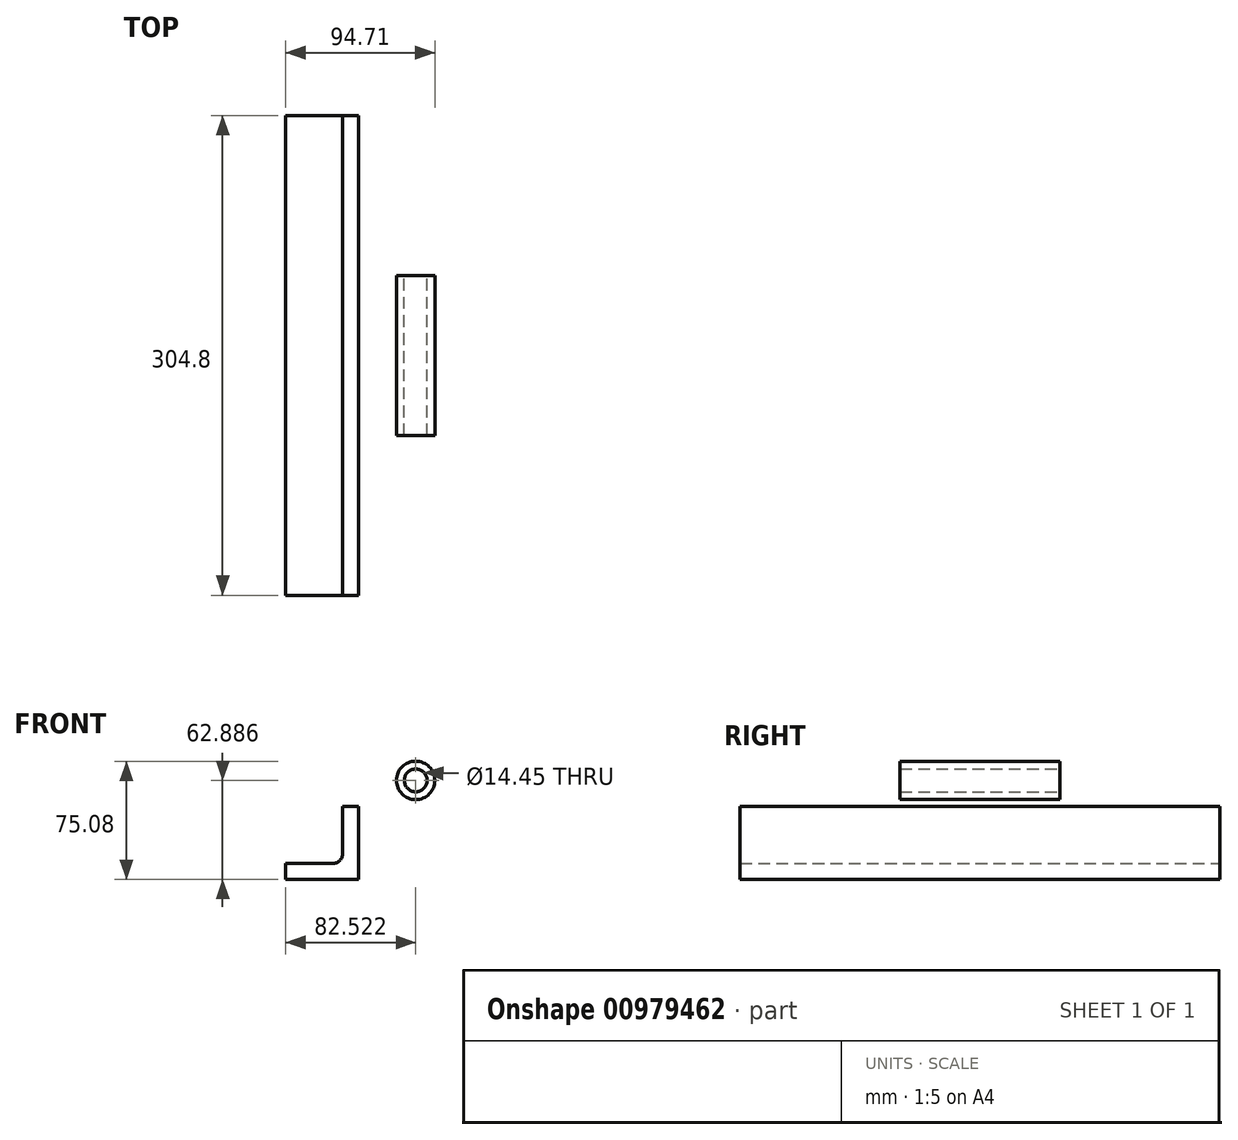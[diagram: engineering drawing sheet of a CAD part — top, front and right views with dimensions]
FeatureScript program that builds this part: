
annotation { "Feature Type Name" : "Feature", "Feature Type Description" : "" }
export const myFeature = defineFeature(function(context is Context, id is Id, definition is map)
    precondition{}
    {
        {
            var Q0;
            Q0=qCreatedBy(makeId("Front.planeOp"),FACE);
            var sketch = newSketch(context, id + "F0", { "sketchPlane" : qUnion([Q0])});
            skLineSegment(sketch, "E0.bottom", {"start": v(-46.24, 10.07) * mm, "end": v(-16.42, 10.07) * mm});
            skLineSegment(sketch, "E0.top", {"start": v(-46.24, 0) * mm, "end": v(0, 0) * mm});
            skLineSegment(sketch, "E0.left", {"start": v(-46.24, 10.07) * mm, "end": v(-46.24, 0) * mm});
            skLineSegment(sketch, "E0.right", {"start": v(0, 10.07) * mm, "end": v(0, 0) * mm});
            skLineSegment(sketch, "E1.bottom", {"start": v(-10.07, 0) * mm, "end": v(0, 0) * mm});
            skLineSegment(sketch, "E1.top", {"start": v(-10.07, 46.24) * mm, "end": v(0, 46.24) * mm});
            skLineSegment(sketch, "E1.left", {"start": v(-10.07, 16.42) * mm, "end": v(-10.07, 46.24) * mm});
            skLineSegment(sketch, "E1.right", {"start": v(0, 0) * mm, "end": v(0, 46.24) * mm});
            skArc(sketch, "E2.filletArc", {"start": v(-16.42, 10.07) * mm, "mid": v(-11.93, 11.93) * mm, "end": v(-10.07, 16.42) * mm});
            skSolve(sketch);
        }
        {
            var Q0;
            Q0=makeQuery(id+"F0.imprint","IMPRINT",FACE,{"disambiguationData":[TD([[makeQuery(id+"F0.imprint","IMPRINT",EDGE,{"derivedFrom":sQuery(id+"F0.wireOp",EDGE,"E0.bottom")}),-1.0]])]});
            extrude(context, id + "F1", {"entities" : qUnion([Q0]), "endBound" : BoundingType.SYMMETRIC, "depth" : 304.8 * mm, "offsetDistance" : 25.4 * mm});
        }
        {
            var Q0;
            Q0=qCreatedBy(makeId("Front.planeOp"),FACE);
            var sketch = newSketch(context, id + "F2", { "sketchPlane" : qUnion([Q0])});
            skCircle(sketch, "E3", {"center": v(36.28, 62.89) * mm, "radius": 7.22 * mm});
            skCircle(sketch, "E4", {"center": v(36.28, 62.89) * mm, "radius": 12.2 * mm});
            skSolve(sketch);
        }
        {
            var Q0;
            Q0 = qSketchRegion(id + "F2", true);
            extrude(context, id + "F3", {"entities" : qUnion([Q0]), "endBound" : BoundingType.SYMMETRIC, "depth" : 101.6 * mm, "offsetDistance" : 25.4 * mm});
        }
    });
